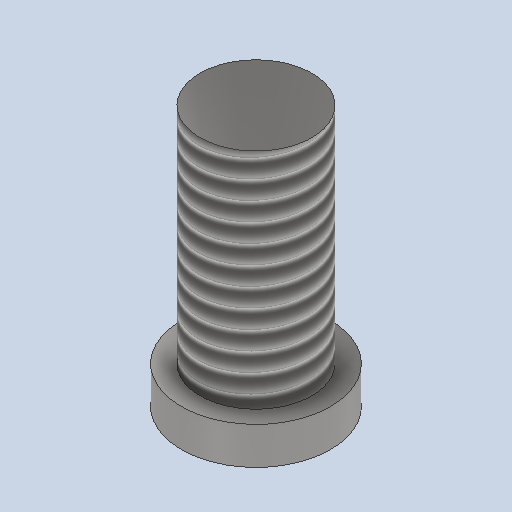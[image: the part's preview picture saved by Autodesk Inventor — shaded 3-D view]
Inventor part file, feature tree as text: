
AUTODESK INVENTOR PART (.ipt)
format: ipt  version: 2022 (Build 260153000, 153)  size: 176,640 bytes
history: native  units: in
note: dims shown in document units (in); Inventor stores cm internally (conversion verified against a paired STEP export)
features: extrude x3, sketch x3, thread x1
ambient origin geometry x8: Origin, YZ Plane, XZ Plane, XY Plane, X Axis, Y Axis, Z Axis, Center Point
bodies: Solid1 (feature_tree)
feature tree (7):
  extrude  "Extrusion1"  Depth=0.2362in TaperAngle=0.0deg
  thread  "Thread1"  [1 undecoded]
  extrude  "Extrusion2"  Depth=0.0394in TaperAngle=0.0deg
  extrude  "Extrusion3"  Depth=0.0295in TaperAngle=0.0deg
  sketch  "Sketch1"  dims[d0=0.1181in d1=0.2362in d2=0.0in d3=0.2362in d4=0.0in]
  sketch  "Sketch2"  dims[d5=0.1575in d6=0.0394in d7=0.0in]
  sketch  "Sketch3"  dims[d8=0.0394in d9=0.0295in d10=0.0in]
note: 1 required parameter value undecoded (feature->parameter linkage not recoverable at this tier; creation-order binding heuristic only, values carry confidence <= 0.55)
